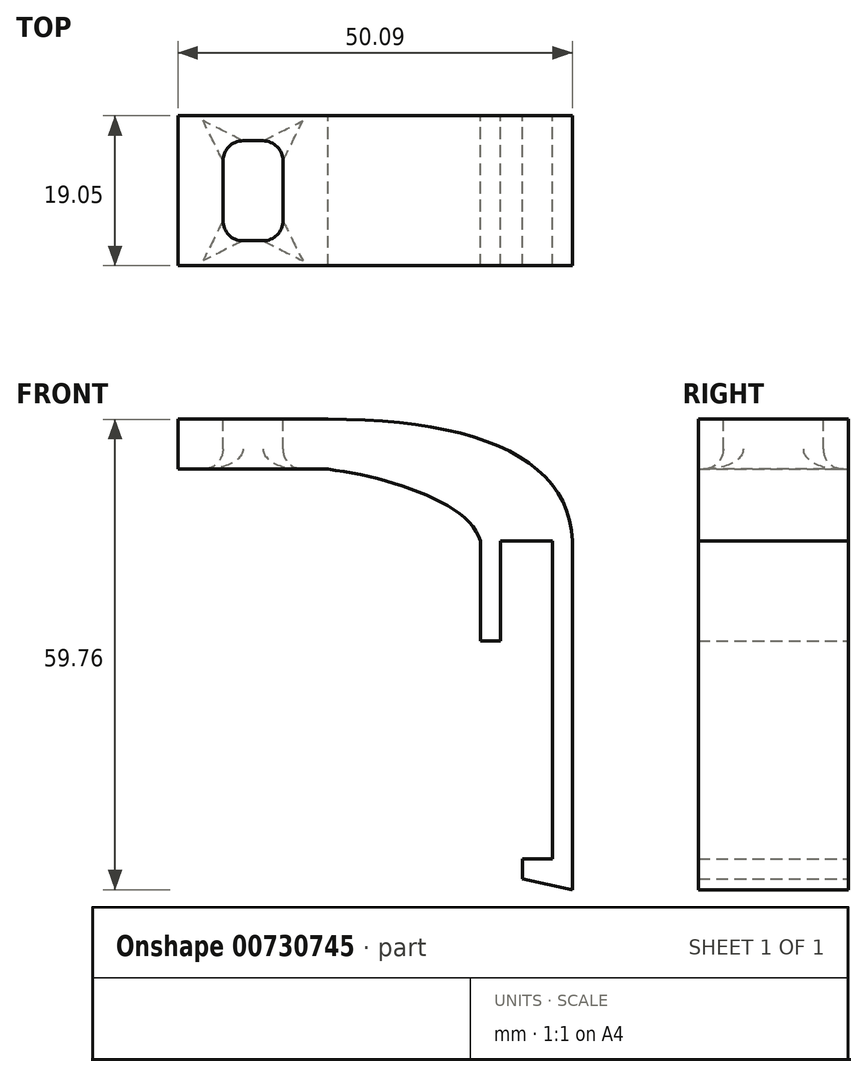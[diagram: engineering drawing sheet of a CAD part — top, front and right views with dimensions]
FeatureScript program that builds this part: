
annotation { "Feature Type Name" : "Feature", "Feature Type Description" : "" }
export const myFeature = defineFeature(function(context is Context, id is Id, definition is map)
    precondition{}
    {
        {
            var Q0;
            Q0=qCreatedBy(makeId("Front.planeOp"),FACE);
            var sketch = newSketch(context, id + "F0", { "sketchPlane" : qUnion([Q0])});
            skLineSegment(sketch, "E0.bottom", {"start": v(12.95, 0.21) * mm, "end": v(6.35, 0.21) * mm});
            skPoint(sketch, "E0.middle", {"position": v(9.65, -6.14) * mm});
            skLineSegment(sketch, "E1.right", {"start": v(15.5, 0.21) * mm, "end": v(15.5, -40.17) * mm});
            skLineSegment(sketch, "E2.bottom", {"start": v(-15.55, 9.34) * mm, "end": v(-34.6, 9.34) * mm});
            skFitSpline(sketch, "E3", {"points": [v(-15.55, 15.7) * mm, v(15.5, 0.21) * mm], "startDerivative": vector(55.67, 0.15) * mm, "endDerivative": vector(0.93, -31.98) * mm});
            skFitSpline(sketch, "E4", {"points": [v(-15.55, 9.34) * mm, v(3.81, 0.21) * mm], "startDerivative": vector(22.48, -2.8) * mm, "endDerivative": vector(3.82, -14.84) * mm});
            skPoint(sketch, "E5.right.end.orphan", {"position": v(3.81, -12.49) * mm});
            skPoint(sketch, "E0.right.end.orphan", {"position": v(6.35, -12.49) * mm});
            skLineSegment(sketch, "E6", {"start": v(12.95, 0.21) * mm, "end": v(12.95, -40.17) * mm});
            skLineSegment(sketch, "E7", {"start": v(12.95, -40.17) * mm, "end": v(9.14, -40.17) * mm});
            skLineSegment(sketch, "E8", {"start": v(9.14, -40.17) * mm, "end": v(9.14, -42.71) * mm});
            skLineSegment(sketch, "E9", {"start": v(9.14, -42.71) * mm, "end": v(15.5, -44.07) * mm});
            skLineSegment(sketch, "E10", {"start": v(15.5, -44.07) * mm, "end": v(15.5, -40.17) * mm});
            skLineSegment(sketch, "E11", {"start": v(6.35, 0.21) * mm, "end": v(6.35, -12.49) * mm});
            skLineSegment(sketch, "E12", {"start": v(3.81, -12.49) * mm, "end": v(3.81, 0.21) * mm});
            skLineSegment(sketch, "E13", {"start": v(3.81, -12.49) * mm, "end": v(6.35, -12.49) * mm});
            skLineSegment(sketch, "E14", {"start": v(-34.6, 9.34) * mm, "end": v(-34.6, 15.7) * mm});
            skLineSegment(sketch, "E15", {"start": v(-34.6, 15.7) * mm, "end": v(-15.55, 15.7) * mm});
            skSolve(sketch);
        }
        {
            var Q0;
            Q0=makeQuery(id+"F0.imprint","IMPRINT",FACE,{"disambiguationData":[TD([[makeQuery(id+"F0.imprint","IMPRINT",EDGE,{"derivedFrom":sQuery(id+"F0.wireOp",EDGE,"E0.bottom")}),-1.0]])]});
            extrude(context, id + "F1", {"entities" : qUnion([Q0]), "depth" : 19.05 * mm, "offsetDistance" : 25.4 * mm});
        }
        {
            var Q0;
            Q0=makeQuery(id+"F1.opExtrude","SWEPT_FACE",FACE,{"disambiguationData":[OSD([sQuery(id+"F0.wireOp",EDGE,"E15")])]});
            var sketch = newSketch(context, id + "F2", { "sketchPlane" : qUnion([Q0])});
            skLineSegment(sketch, "E16.bottom", {"start": v(-21.27, -15.88) * mm, "end": v(-28.89, -15.88) * mm});
            skLineSegment(sketch, "E16.top", {"start": v(-21.27, -3.18) * mm, "end": v(-28.89, -3.18) * mm});
            skLineSegment(sketch, "E16.left", {"start": v(-21.27, -15.88) * mm, "end": v(-21.27, -3.18) * mm});
            skLineSegment(sketch, "E16.right", {"start": v(-28.89, -15.88) * mm, "end": v(-28.89, -3.18) * mm});
            skPoint(sketch, "E16.middle", {"position": v(-25.08, -9.53) * mm});
            skLineSegment(sketch, "E17.bottom", {"start": v(-17.46, -17.15) * mm, "end": v(-32.7, -17.15) * mm});
            skLineSegment(sketch, "E17.top", {"start": v(-17.46, -1.9) * mm, "end": v(-32.7, -1.9) * mm});
            skLineSegment(sketch, "E17.left", {"start": v(-17.46, -17.15) * mm, "end": v(-17.46, -1.9) * mm});
            skLineSegment(sketch, "E17.right", {"start": v(-32.7, -17.15) * mm, "end": v(-32.7, -1.9) * mm});
            skSolve(sketch);
        }
        {
            var Q0;
            Q0=makeQuery(id+"F2.imprint","IMPRINT",FACE,{"disambiguationData":[TD([[makeQuery(id+"F2.imprint","IMPRINT",EDGE,{"derivedFrom":sQuery(id+"F2.wireOp",EDGE,"E16.bottom")}),-1.0]])]});
            extrude(context, id + "F3", {"entities" : qUnion([Q0]), "operationType" : NewBodyOperationType.REMOVE, "oppositeDirection" : true, "depth" : 25.4 * mm, "offsetDistance" : 25.4 * mm});
        }
        {
            var Q0;
            Q0=makeQuery(id+"F3.boolean.opBoolean","INTERSECT",EDGE,{"derivedFrom":[makeQuery(id+"F1.opExtrude","SWEPT_FACE",FACE,{"disambiguationData":[OSD([sQuery(id+"F0.wireOp",EDGE,"E2.bottom")])]}),makeQuery(id+"F3.opExtrude","SWEPT_FACE",FACE,{"disambiguationData":[OSD([sQuery(id+"F2.wireOp",EDGE,"E16.top")])]})]});
            var Q1;
            Q1=makeQuery(id+"F3.boolean.opBoolean","INTERSECT",EDGE,{"derivedFrom":[makeQuery(id+"F1.opExtrude","SWEPT_FACE",FACE,{"disambiguationData":[OSD([sQuery(id+"F0.wireOp",EDGE,"E2.bottom")])]}),makeQuery(id+"F3.opExtrude","SWEPT_FACE",FACE,{"disambiguationData":[OSD([sQuery(id+"F2.wireOp",EDGE,"E16.left")])]})]});
            var Q2;
            Q2=makeQuery(id+"F3.boolean.opBoolean","INTERSECT",EDGE,{"derivedFrom":[makeQuery(id+"F1.opExtrude","SWEPT_FACE",FACE,{"disambiguationData":[OSD([sQuery(id+"F0.wireOp",EDGE,"E2.bottom")])]}),makeQuery(id+"F3.opExtrude","SWEPT_FACE",FACE,{"disambiguationData":[OSD([sQuery(id+"F2.wireOp",EDGE,"E16.right")])]})]});
            var Q3;
            Q3=makeQuery(id+"F3.boolean.opBoolean","INTERSECT",EDGE,{"derivedFrom":[makeQuery(id+"F1.opExtrude","SWEPT_FACE",FACE,{"disambiguationData":[OSD([sQuery(id+"F0.wireOp",EDGE,"E2.bottom")])]}),makeQuery(id+"F3.opExtrude","SWEPT_FACE",FACE,{"disambiguationData":[OSD([sQuery(id+"F2.wireOp",EDGE,"E16.bottom")])]})]});
            var Q4;
            Q4=makeQuery(id+"F3.boolean.opBoolean","COPY",EDGE,{"derivedFrom":makeQuery(id+"F3.opExtrude","CAP_EDGE",EDGE,{"disambiguationData":[OSD([sQuery(id+"F2.wireOp",EDGE,"E16.left")])],"isStart":true})});
            var Q5;
            Q5=makeQuery(id+"F3.boolean.opBoolean","COPY",EDGE,{"derivedFrom":makeQuery(id+"F3.opExtrude","CAP_EDGE",EDGE,{"disambiguationData":[OSD([sQuery(id+"F2.wireOp",EDGE,"E16.top")])],"isStart":true})});
            var Q6;
            Q6=makeQuery(id+"F3.boolean.opBoolean","COPY",EDGE,{"derivedFrom":makeQuery(id+"F3.opExtrude","CAP_EDGE",EDGE,{"disambiguationData":[OSD([sQuery(id+"F2.wireOp",EDGE,"E16.right")])],"isStart":true})});
            var Q7;
            Q7=makeQuery(id+"F3.boolean.opBoolean","COPY",EDGE,{"derivedFrom":makeQuery(id+"F3.opExtrude","CAP_EDGE",EDGE,{"disambiguationData":[OSD([sQuery(id+"F2.wireOp",EDGE,"E16.bottom")])],"isStart":true})});
            fillet(context, id + "F4", {"entities" : qUnion([Q0, Q1, Q2, Q3, Q4, Q5, Q6, Q7]), "radius" : 2.54 * mm, "tangentPropagation" : true, "allowEdgeOverflow" : false});
        }
        {
            var Q0;
            Q0=makeQuery(id+"F3.boolean.opBoolean","COPY",EDGE,{"derivedFrom":makeQuery(id+"F3.opExtrude","SWEPT_EDGE",EDGE,{"disambiguationData":[OSD([sQuery(id+"F2.wireOp",EDGE,"E16.bottom"),sQuery(id+"F2.wireOp",EDGE,"E16.right")])]})});
            var Q1;
            Q1=makeQuery(id+"F3.boolean.opBoolean","COPY",EDGE,{"derivedFrom":makeQuery(id+"F3.opExtrude","SWEPT_EDGE",EDGE,{"disambiguationData":[OSD([sQuery(id+"F2.wireOp",EDGE,"E16.bottom"),sQuery(id+"F2.wireOp",EDGE,"E16.left")])]})});
            var Q2;
            Q2=makeQuery(id+"F3.boolean.opBoolean","COPY",EDGE,{"derivedFrom":makeQuery(id+"F3.opExtrude","SWEPT_EDGE",EDGE,{"disambiguationData":[OSD([sQuery(id+"F2.wireOp",EDGE,"E16.top"),sQuery(id+"F2.wireOp",EDGE,"E16.left")])]})});
            var Q3;
            Q3=makeQuery(id+"F3.boolean.opBoolean","COPY",EDGE,{"derivedFrom":makeQuery(id+"F3.opExtrude","SWEPT_EDGE",EDGE,{"disambiguationData":[OSD([sQuery(id+"F2.wireOp",EDGE,"E16.top"),sQuery(id+"F2.wireOp",EDGE,"E16.right")])]})});
            fillet(context, id + "F5", {"entities" : qUnion([Q0, Q1, Q2, Q3]), "radius" : 2.54 * mm, "tangentPropagation" : true, "allowEdgeOverflow" : false});
        }
    });
